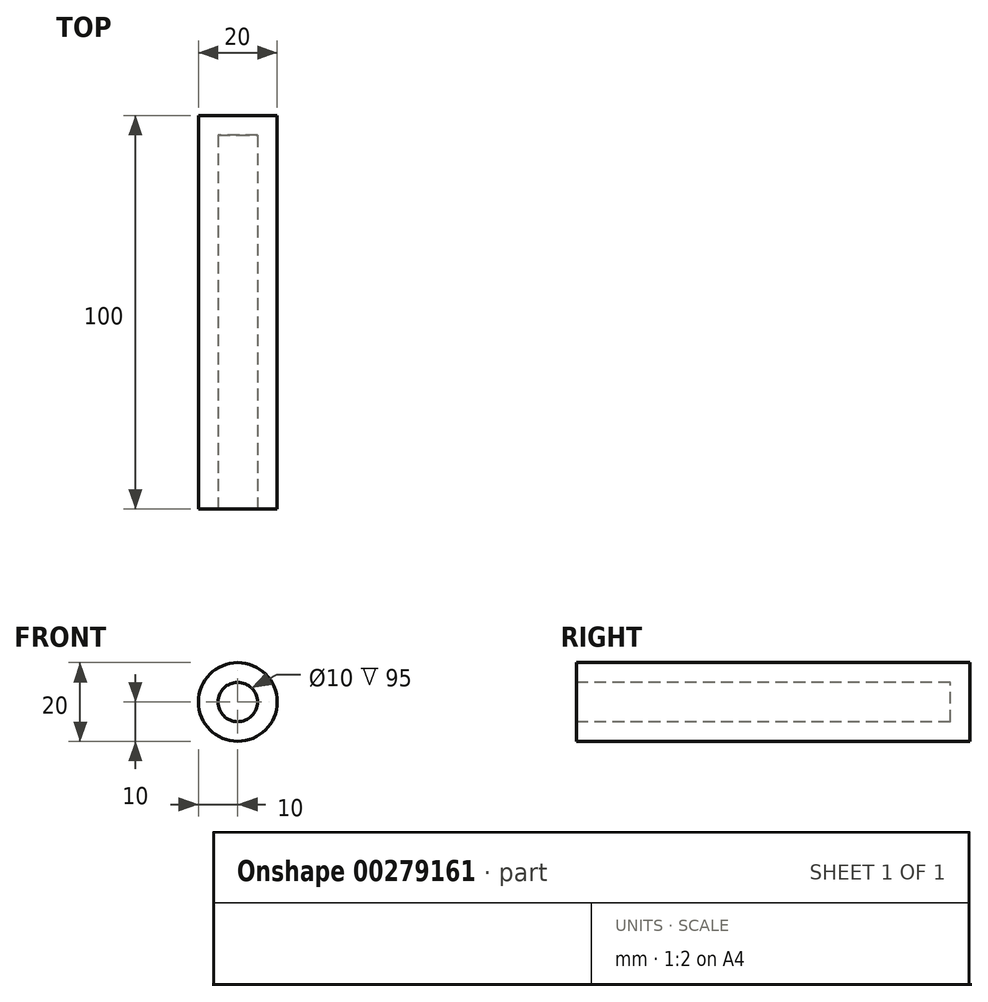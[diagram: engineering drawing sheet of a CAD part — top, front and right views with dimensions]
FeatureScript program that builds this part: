
annotation { "Feature Type Name" : "Feature", "Feature Type Description" : "" }
export const myFeature = defineFeature(function(context is Context, id is Id, definition is map)
    precondition{}
    {
        {
            var Q0;
            Q0=qCreatedBy(makeId("Right.planeOp"),FACE);
            var sketch = newSketch(context, id + "F0", { "sketchPlane" : qUnion([Q0])});
            skLineSegment(sketch, "E0", {"start": v(0, 5) * mm, "end": v(100, 5) * mm});
            skLineSegment(sketch, "E1.0", {"start": v(0, 10) * mm, "end": v(100, 10) * mm});
            skLineSegment(sketch, "E2", {"start": v(0, 10) * mm, "end": v(0, 5) * mm});
            skLineSegment(sketch, "E3", {"start": v(100, 5) * mm, "end": v(100, 10) * mm});
            skLineSegment(sketch, "E4", {"start": v(95, 5) * mm, "end": v(95, 0) * mm});
            skLineSegment(sketch, "E5", {"start": v(100, 0) * mm, "end": v(100, 5) * mm});
            skLineSegment(sketch, "E6", {"start": v(95, 0) * mm, "end": v(100, 0) * mm});
            skSolve(sketch);
        }
        {
            var Q0;
            {var subQ2=sQuery(id+"F0.wireOp",EDGE,"E4");Q0=makeQuery(id+"F0.imprint","IMPRINT",FACE,{"disambiguationData":[TD([[makeQuery(id+"F0.imprint","IMPRINT",EDGE,{"derivedFrom":subQ2}),1.0]])]});}
            var Q1;
            Q1=makeQuery(id+"F0.imprint","IMPRINT",FACE,{"disambiguationData":[TD([[makeQuery(id+"F0.imprint","IMPRINT",EDGE,{"derivedFrom":sQuery(id+"F0.wireOp",EDGE,"E1.0")}),-1.0]])]});
            var Q2;
            Q2=sQuery(id+"F0.wireOp",EDGE,"E6");
            revolve(context, id + "F1", {"entities" : qUnion([Q0, Q1]), "axis" : qUnion([Q2]), "revolveType" : RevolveType.FULL});
        }
    });
